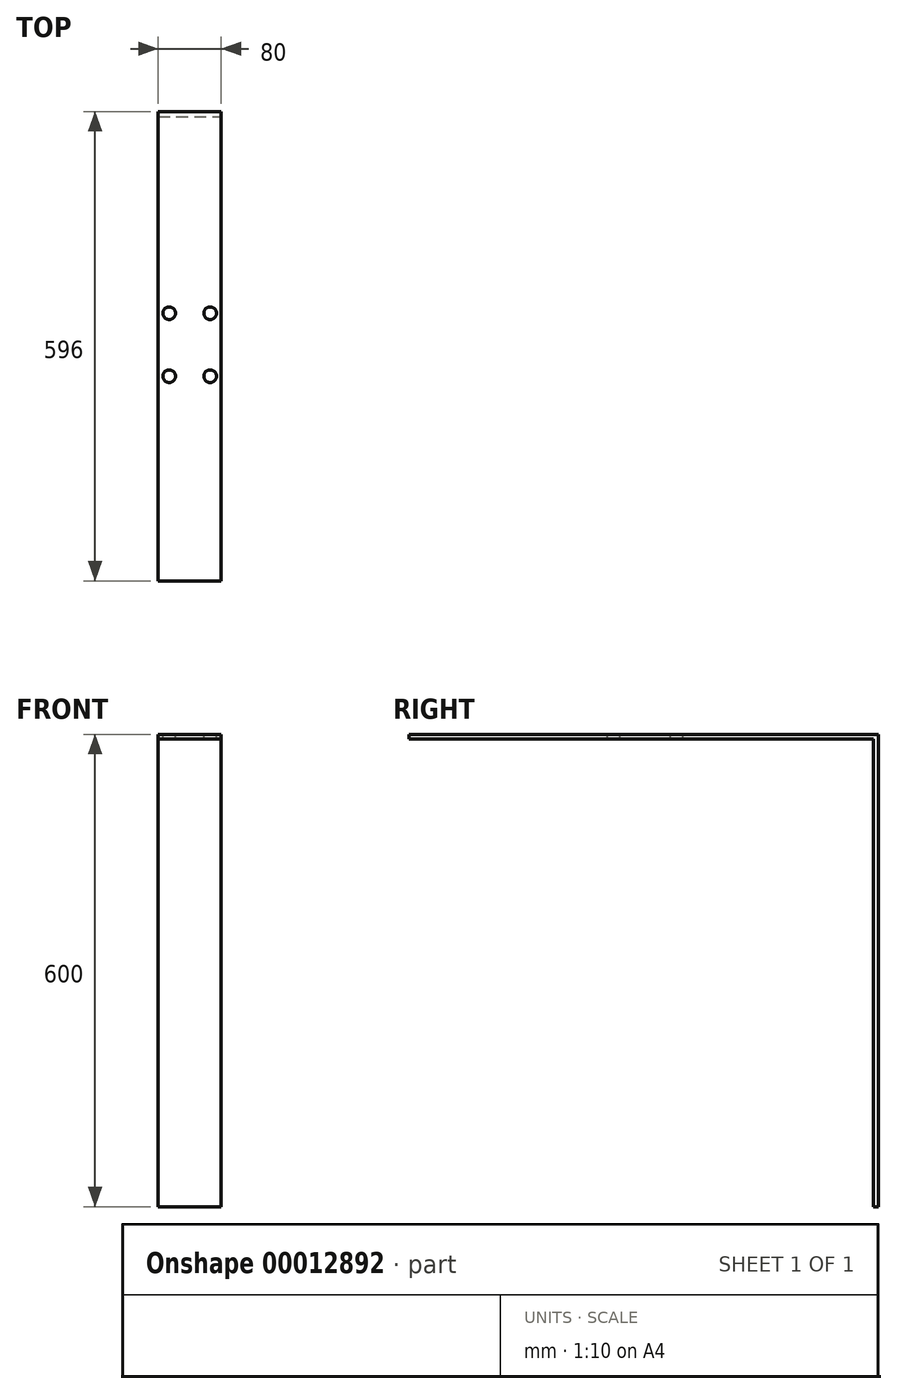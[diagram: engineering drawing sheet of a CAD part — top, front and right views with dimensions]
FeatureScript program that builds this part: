
annotation { "Feature Type Name" : "Feature", "Feature Type Description" : "" }
export const myFeature = defineFeature(function(context is Context, id is Id, definition is map)
    precondition{}
    {
        {
            var Q0;
            Q0=qCreatedBy(makeId("Front.planeOp"),FACE);
            var sketch = newSketch(context, id + "F0", { "sketchPlane" : qUnion([Q0])});
            skLineSegment(sketch, "E0.bottom", {"start": v(-37.97, 534) * mm, "end": v(42.03, 534) * mm});
            skLineSegment(sketch, "E0.top", {"start": v(-37.97, -66) * mm, "end": v(42.03, -66) * mm});
            skLineSegment(sketch, "E0.left", {"start": v(-37.97, 534) * mm, "end": v(-37.97, -66) * mm});
            skLineSegment(sketch, "E0.right", {"start": v(42.03, 534) * mm, "end": v(42.03, -66) * mm});
            skSolve(sketch);
        }
        {
            var Q0;
            Q0=makeQuery(id+"F0.imprint","IMPRINT",FACE,{"disambiguationData":[TD([[makeQuery(id+"F0.imprint","IMPRINT",EDGE,{"derivedFrom":sQuery(id+"F0.wireOp",EDGE,"E0.bottom")}),-1.0]])]});
            extrude(context, id + "F1", {"entities" : qUnion([Q0]), "depth" : 6 * mm});
        }
        {
            var Q0;
            Q0=makeQuery(id+"F1.opExtrude","CAP_FACE",FACE,{"disambiguationData":[OSD([sQuery(id+"F0.wireOp",EDGE,"E0.bottom"),sQuery(id+"F0.wireOp",EDGE,"E0.top"),sQuery(id+"F0.wireOp",EDGE,"E0.left"),sQuery(id+"F0.wireOp",EDGE,"E0.right")])],"isStart":false});
            var sketch = newSketch(context, id + "F2", { "sketchPlane" : qUnion([Q0])});
            skLineSegment(sketch, "E1.bottom", {"start": v(-37.97, 534) * mm, "end": v(42.03, 534) * mm});
            skLineSegment(sketch, "E1.top", {"start": v(-37.97, 528) * mm, "end": v(42.03, 528) * mm});
            skLineSegment(sketch, "E1.left", {"start": v(-37.97, 534) * mm, "end": v(-37.97, 528) * mm});
            skLineSegment(sketch, "E1.right", {"start": v(42.03, 534) * mm, "end": v(42.03, 528) * mm});
            skSolve(sketch);
        }
        {
            var Q0;
            Q0=makeQuery(id+"F2.imprint","IMPRINT",FACE,{"disambiguationData":[TD([[makeQuery(id+"F2.imprint","IMPRINT",EDGE,{"derivedFrom":sQuery(id+"F2.wireOp",EDGE,"E1.bottom")}),-1.0]])]});
            extrude(context, id + "F3", {"entities" : qUnion([Q0]), "operationType" : NewBodyOperationType.ADD, "depth" : 590 * mm});
        }
        {
            var Q0;
            Q0=makeQuery(id+"F3.boolean.opBoolean","MERGE",FACE,{"derivedFrom":[makeQuery(id+"F1.opExtrude","SWEPT_FACE",FACE,{"disambiguationData":[OSD([sQuery(id+"F0.wireOp",EDGE,"E0.bottom")])]}),makeQuery(id+"F3.opExtrude","SWEPT_FACE",FACE,{"disambiguationData":[OSD([sQuery(id+"F2.wireOp",EDGE,"E1.bottom")])]})]});
            var sketch = newSketch(context, id + "F4", { "sketchPlane" : qUnion([Q0])});
            skLineSegment(sketch, "E2", {"start": v(161.12, -296) * mm, "end": v(-206.26, -296) * mm, "construction": true});
            skPoint(sketch, "E3", {"position": v(28.03, -256) * mm});
            skPoint(sketch, "E4", {"position": v(28.03, -336) * mm});
            skPoint(sketch, "E5", {"position": v(-23.97, -336) * mm});
            skPoint(sketch, "E6", {"position": v(-23.97, -256) * mm});
            skSolve(sketch);
        }
        {
            var Q0;
            Q0=sQuery(id+"F4.wireOp",VERTEX,"E4");
            var Q1;
            Q1=sQuery(id+"F4.wireOp",VERTEX,"E5");
            var Q2;
            Q2=sQuery(id+"F4.wireOp",VERTEX,"E6");
            var Q3;
            Q3=sQuery(id+"F4.wireOp",VERTEX,"E3");
            var Q4;
            Q4=makeQuery(id+"F1.opExtrude","SWEPT_BODY",BODY,{"disambiguationData":[OSD([sQuery(id+"F0.wireOp",EDGE,"E0.bottom"),sQuery(id+"F0.wireOp",EDGE,"E0.top"),sQuery(id+"F0.wireOp",EDGE,"E0.left"),sQuery(id+"F0.wireOp",EDGE,"E0.right")])]});
            hole(context, id + "F5", {"style" : HoleStyle.SIMPLE, "holeDiameter" : 16 * mm, "endStyle" : HoleEndStyle.THROUGH, "locations" : qUnion([Q0, Q1, Q2, Q3]), "scope" : qUnion([Q4])});
        }
    });
